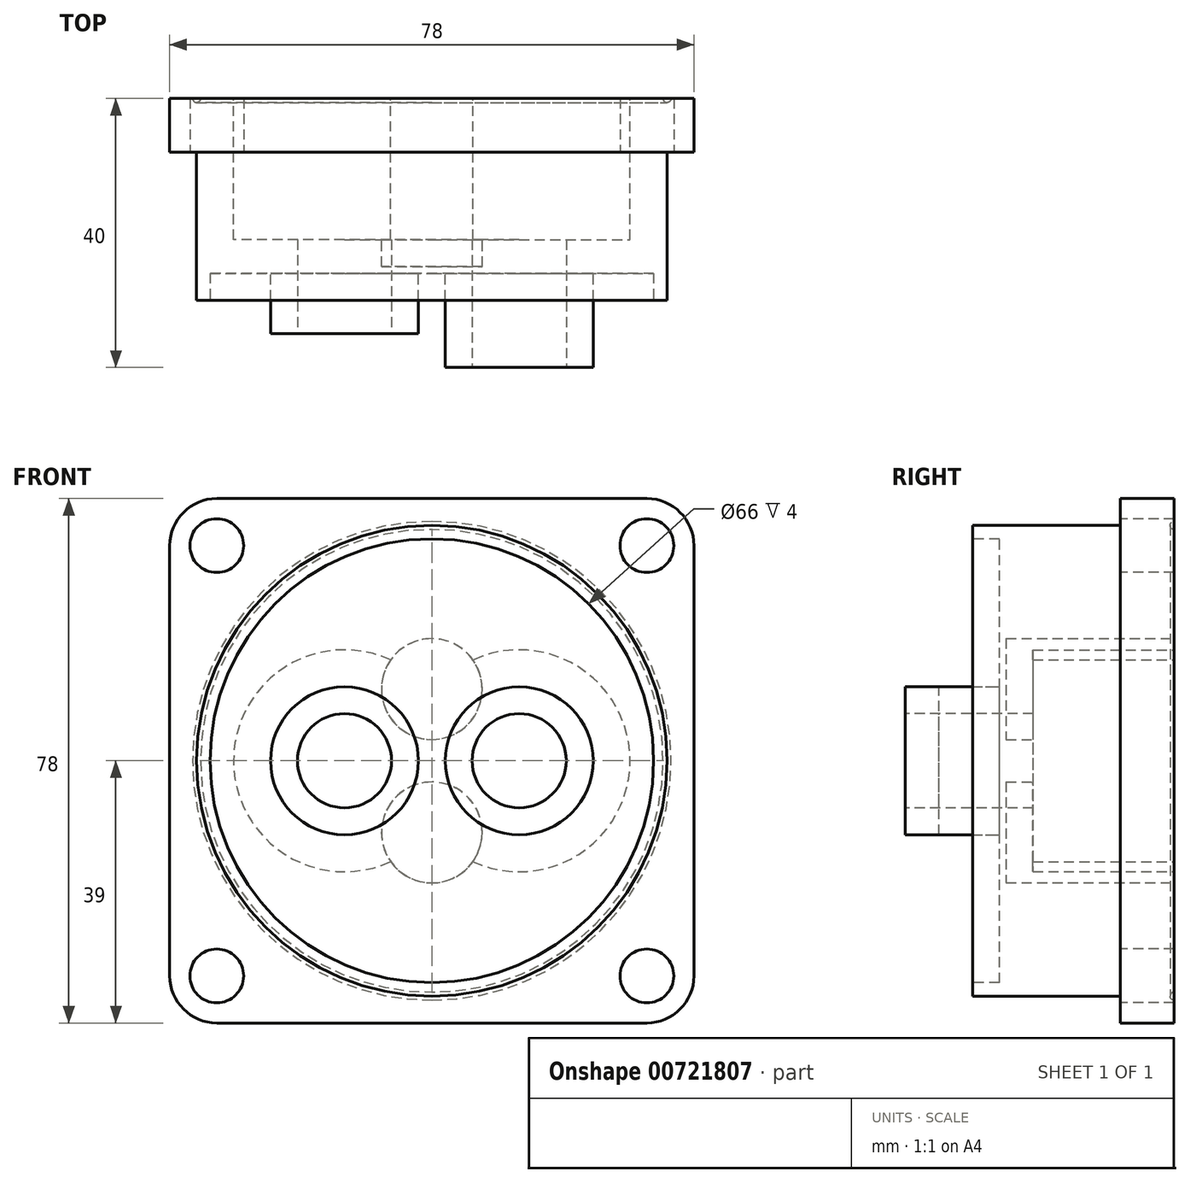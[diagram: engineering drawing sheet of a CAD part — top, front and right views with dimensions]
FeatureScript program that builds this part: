
annotation { "Feature Type Name" : "Feature", "Feature Type Description" : "" }
export const myFeature = defineFeature(function(context is Context, id is Id, definition is map)
    precondition{}
    {
        {
            var Q0;
            Q0=qCreatedBy(makeId("Front.planeOp"),FACE);
            var sketch = newSketch(context, id + "F0", { "sketchPlane" : qUnion([Q0])});
            skLineSegment(sketch, "E0.bottom", {"start": v(-39, 0) * mm, "end": v(39, 0) * mm});
            skLineSegment(sketch, "E0.top", {"start": v(-39, 78) * mm, "end": v(39, 78) * mm});
            skLineSegment(sketch, "E0.left", {"start": v(-39, 0) * mm, "end": v(-39, 78) * mm});
            skLineSegment(sketch, "E0.right", {"start": v(39, 0) * mm, "end": v(39, 78) * mm});
            skSolve(sketch);
        }
        {
            var Q0;
            Q0 = qSketchRegion(id + "F0", true);
            extrude(context, id + "F1", {"entities" : qUnion([Q0]), "depth" : 8 * mm, "offsetDistance" : 25 * mm});
        }
        {
            var Q0;
            Q0=makeQuery(id+"F1.opExtrude","SWEPT_EDGE",EDGE,{"disambiguationData":[OSD([sQuery(id+"F0.wireOp",EDGE,"E0.top"),sQuery(id+"F0.wireOp",EDGE,"E0.left")])]});
            var Q1;
            Q1=makeQuery(id+"F1.opExtrude","SWEPT_EDGE",EDGE,{"disambiguationData":[OSD([sQuery(id+"F0.wireOp",EDGE,"E0.top"),sQuery(id+"F0.wireOp",EDGE,"E0.right")])]});
            var Q2;
            Q2=makeQuery(id+"F1.opExtrude","SWEPT_EDGE",EDGE,{"disambiguationData":[OSD([sQuery(id+"F0.wireOp",EDGE,"E0.bottom"),sQuery(id+"F0.wireOp",EDGE,"E0.right")])]});
            var Q3;
            Q3=makeQuery(id+"F1.opExtrude","SWEPT_EDGE",EDGE,{"disambiguationData":[OSD([sQuery(id+"F0.wireOp",EDGE,"E0.bottom"),sQuery(id+"F0.wireOp",EDGE,"E0.left")])]});
            fillet(context, id + "F2", {"entities" : qUnion([Q0, Q1, Q2, Q3]), "radius" : 7 * mm, "tangentPropagation" : true, "allowEdgeOverflow" : false});
        }
        {
            var Q0;
            Q0=makeQuery(id+"F1.opExtrude","CAP_FACE",FACE,{"disambiguationData":[OSD([sQuery(id+"F0.wireOp",EDGE,"E0.bottom"),sQuery(id+"F0.wireOp",EDGE,"E0.top"),sQuery(id+"F0.wireOp",EDGE,"E0.left"),sQuery(id+"F0.wireOp",EDGE,"E0.right")])],"isStart":false});
            var sketch = newSketch(context, id + "F3", { "sketchPlane" : qUnion([Q0])});
            skCircle(sketch, "E1", {"center": v(-32, 71) * mm, "radius": 4 * mm});
            skCircle(sketch, "E2", {"center": v(32, 71) * mm, "radius": 4 * mm});
            skCircle(sketch, "E3", {"center": v(-32, 7) * mm, "radius": 4 * mm});
            skCircle(sketch, "E4", {"center": v(32, 7) * mm, "radius": 4 * mm});
            skCircle(sketch, "E5", {"center": v(0, 39) * mm, "radius": 35 * mm});
            skSolve(sketch);
        }
        {
            var Q0;
            Q0=makeQuery(id+"F3.imprint","IMPRINT",FACE,{"disambiguationData":[TD([[makeQuery(id+"F3.imprint","IMPRINT",EDGE,{"derivedFrom":sQuery(id+"F3.wireOp",EDGE,"E1")}),1.0]])]});
            var Q1;
            Q1=makeQuery(id+"F3.imprint","IMPRINT",FACE,{"disambiguationData":[TD([[makeQuery(id+"F3.imprint","IMPRINT",EDGE,{"derivedFrom":sQuery(id+"F3.wireOp",EDGE,"E2")}),1.0]])]});
            var Q2;
            Q2=makeQuery(id+"F3.imprint","IMPRINT",FACE,{"disambiguationData":[TD([[makeQuery(id+"F3.imprint","IMPRINT",EDGE,{"derivedFrom":sQuery(id+"F3.wireOp",EDGE,"E3")}),1.0]])]});
            var Q3;
            Q3=makeQuery(id+"F3.imprint","IMPRINT",FACE,{"disambiguationData":[TD([[makeQuery(id+"F3.imprint","IMPRINT",EDGE,{"derivedFrom":sQuery(id+"F3.wireOp",EDGE,"E4")}),1.0]])]});
            extrude(context, id + "F4", {"entities" : qUnion([Q0, Q1, Q2, Q3]), "operationType" : NewBodyOperationType.REMOVE, "endBound" : BoundingType.THROUGH_ALL, "oppositeDirection" : true, "depth" : 21 * mm, "offsetDistance" : 25 * mm});
        }
        {
            var Q0;
            Q0=makeQuery(id+"F1.opExtrude","CAP_FACE",FACE,{"disambiguationData":[OSD([sQuery(id+"F0.wireOp",EDGE,"E0.bottom"),sQuery(id+"F0.wireOp",EDGE,"E0.top"),sQuery(id+"F0.wireOp",EDGE,"E0.left"),sQuery(id+"F0.wireOp",EDGE,"E0.right")])],"isStart":false});
            var sketch = newSketch(context, id + "F5", { "sketchPlane" : qUnion([Q0])});
            skCircle(sketch, "E6", {"center": v(0, 39) * mm, "radius": 35 * mm});
            skSolve(sketch);
        }
        {
            var Q0;
            Q0=makeQuery(id+"F5.imprint","IMPRINT",FACE,{"disambiguationData":[TD([[makeQuery(id+"F5.imprint","IMPRINT",EDGE,{"derivedFrom":sQuery(id+"F5.wireOp",EDGE,"E6")}),1.0]])]});
            var Q1;
            Q1=sQuery(id+"F5.wireOp",EDGE,"E6");
            extrude(context, id + "F6", {"entities" : qUnion([Q0]), "operationType" : NewBodyOperationType.ADD, "surfaceEntities" : qUnion([Q1]), "depth" : 22 * mm, "offsetDistance" : 25 * mm});
        }
        {
            var Q0;
            Q0=makeQuery(id+"F6.opExtrude","CAP_FACE",FACE,{"disambiguationData":[OSD([sQuery(id+"F5.wireOp",EDGE,"E6")])],"isStart":false});
            var sketch = newSketch(context, id + "F7", { "sketchPlane" : qUnion([Q0])});
            skCircle(sketch, "E7", {"center": v(0, 39) * mm, "radius": 33 * mm});
            skSolve(sketch);
        }
        {
            var Q0;
            Q0=makeQuery(id+"F7.imprint","IMPRINT",FACE,{"disambiguationData":[TD([[makeQuery(id+"F7.imprint","IMPRINT",EDGE,{"derivedFrom":sQuery(id+"F7.wireOp",EDGE,"E7")}),1.0]])]});
            extrude(context, id + "F8", {"entities" : qUnion([Q0]), "operationType" : NewBodyOperationType.REMOVE, "oppositeDirection" : true, "depth" : 4 * mm, "offsetDistance" : 25 * mm});
        }
        {
            var Q0;
            Q0=makeQuery(id+"F1.opExtrude","CAP_FACE",FACE,{"disambiguationData":[OSD([sQuery(id+"F0.wireOp",EDGE,"E0.bottom"),sQuery(id+"F0.wireOp",EDGE,"E0.top"),sQuery(id+"F0.wireOp",EDGE,"E0.left"),sQuery(id+"F0.wireOp",EDGE,"E0.right")])],"isStart":true});
            var sketch = newSketch(context, id + "F9", { "sketchPlane" : qUnion([Q0])});
            skCircle(sketch, "E8", {"center": v(0, 39) * mm, "radius": 35 * mm});
            skSolve(sketch);
        }
        {
            var Q0;
            Q0=qCreatedBy(makeId("Right.planeOp"),FACE);
            var sketch = newSketch(context, id + "F10", { "sketchPlane" : qUnion([Q0])});
            skCircle(sketch, "E9", {"center": v(0, 74) * mm, "radius": 0.6 * mm});
            skLineSegment(sketch, "E10", {"start": v(0, 74.39) * mm, "end": v(0, 73.61) * mm});
            skSolve(sketch);
        }
        {
            var Q0;
            Q0 = qSketchRegion(id + "F10", true);
            var Q1;
            Q1=sQuery(id+"F9.wireOp",EDGE,"E8");
            sweep(context, id + "F11", {"operationType" : NewBodyOperationType.REMOVE, "profiles" : qUnion([Q0]), "path" : qUnion([Q1])});
        }
        {
            var Q0;
            Q0=makeQuery(id+"F11.boolean.opBoolean","SPLIT",FACE,{"disambiguationData":[TD([makeQuery(id+"F11.opSweep","SWEPT_FACE",FACE,{"disambiguationData":[OSD([sQuery(id+"F9.wireOp",EDGE,"E8"),sQuery(id+"F10.wireOp",EDGE,"E9")])]})])],"derivedFrom":makeQuery(id+"F1.opExtrude","CAP_FACE",FACE,{"disambiguationData":[OSD([sQuery(id+"F0.wireOp",EDGE,"E0.bottom"),sQuery(id+"F0.wireOp",EDGE,"E0.top"),sQuery(id+"F0.wireOp",EDGE,"E0.left"),sQuery(id+"F0.wireOp",EDGE,"E0.right")])],"isStart":true})});
            var sketch = newSketch(context, id + "F12", { "sketchPlane" : qUnion([Q0])});
            skCircle(sketch, "E11", {"center": v(13, 39) * mm, "radius": 16.5 * mm});
            skCircle(sketch, "E12.MirrorC", {"center": v(-13, 39) * mm, "radius": 16.5 * mm});
            skPoint(sketch, "E13", {"position": v(0, 49.16) * mm});
            skPoint(sketch, "E14", {"position": v(0, 28.84) * mm});
            skPoint(sketch, "E15", {"position": v(-1.86, 51.17) * mm});
            skSolve(sketch);
        }
        {
            var Q0;
            Q0 = qSketchRegion(id + "F12", true);
            extrude(context, id + "F13", {"entities" : qUnion([Q0]), "operationType" : NewBodyOperationType.REMOVE, "oppositeDirection" : true, "depth" : 21 * mm, "offsetDistance" : 25 * mm});
        }
        {
            var Q0;
            Q0=makeQuery(id+"F11.boolean.opBoolean","SPLIT",FACE,{"disambiguationData":[TD([makeQuery(id+"F11.opSweep","SWEPT_FACE",FACE,{"disambiguationData":[OSD([sQuery(id+"F9.wireOp",EDGE,"E8"),sQuery(id+"F10.wireOp",EDGE,"E9")])]})])],"derivedFrom":makeQuery(id+"F1.opExtrude","CAP_FACE",FACE,{"disambiguationData":[OSD([sQuery(id+"F0.wireOp",EDGE,"E0.bottom"),sQuery(id+"F0.wireOp",EDGE,"E0.top"),sQuery(id+"F0.wireOp",EDGE,"E0.left"),sQuery(id+"F0.wireOp",EDGE,"E0.right")])],"isStart":true})});
            var sketch = newSketch(context, id + "F14", { "sketchPlane" : qUnion([Q0])});
            skCircle(sketch, "E16", {"center": v(0, 28.34) * mm, "radius": 7.5 * mm});
            skCircle(sketch, "E17", {"center": v(0, 49.66) * mm, "radius": 7.5 * mm});
            skSolve(sketch);
        }
        {
            var Q0;
            Q0 = qSketchRegion(id + "F14", true);
            extrude(context, id + "F15", {"entities" : qUnion([Q0]), "operationType" : NewBodyOperationType.REMOVE, "oppositeDirection" : true, "depth" : 25 * mm, "offsetDistance" : 25 * mm});
        }
        {
            var Q0;
            Q0=makeQuery(id+"F8.boolean.opBoolean","COPY",FACE,{"derivedFrom":makeQuery(id+"F8.opExtrude","CAP_FACE",FACE,{"disambiguationData":[OSD([sQuery(id+"F7.wireOp",EDGE,"E7")])],"isStart":false})});
            var sketch = newSketch(context, id + "F16", { "sketchPlane" : qUnion([Q0])});
            skCircle(sketch, "E18", {"center": v(13, 39) * mm, "radius": 11 * mm});
            skSolve(sketch);
        }
        {
            var Q0;
            Q0=makeQuery(id+"F16.imprint","IMPRINT",FACE,{"disambiguationData":[TD([[makeQuery(id+"F16.imprint","IMPRINT",EDGE,{"derivedFrom":sQuery(id+"F16.wireOp",EDGE,"E18")}),1.0]])]});
            extrude(context, id + "F17", {"entities" : qUnion([Q0]), "operationType" : NewBodyOperationType.ADD, "depth" : 14 * mm, "offsetDistance" : 25 * mm});
        }
        {
            var Q0;
            Q0=makeQuery(id+"F8.boolean.opBoolean","COPY",FACE,{"derivedFrom":makeQuery(id+"F8.opExtrude","CAP_FACE",FACE,{"disambiguationData":[OSD([sQuery(id+"F7.wireOp",EDGE,"E7")])],"isStart":false})});
            var sketch = newSketch(context, id + "F18", { "sketchPlane" : qUnion([Q0])});
            skCircle(sketch, "E19", {"center": v(-13, 39) * mm, "radius": 11 * mm});
            skSolve(sketch);
        }
        {
            var Q0;
            Q0 = qSketchRegion(id + "F18", true);
            extrude(context, id + "F19", {"entities" : qUnion([Q0]), "operationType" : NewBodyOperationType.ADD, "depth" : 9 * mm, "offsetDistance" : 25 * mm});
        }
        {
            var Q0;
            Q0=makeQuery(id+"F19.opExtrude","CAP_FACE",FACE,{"disambiguationData":[OSD([sQuery(id+"F18.wireOp",EDGE,"E19")])],"isStart":false});
            var sketch = newSketch(context, id + "F20", { "sketchPlane" : qUnion([Q0])});
            skCircle(sketch, "E20", {"center": v(-13, 39) * mm, "radius": 7 * mm});
            skSolve(sketch);
        }
        {
            var Q0;
            Q0=makeQuery(id+"F20.imprint","IMPRINT",FACE,{"disambiguationData":[TD([[makeQuery(id+"F20.imprint","IMPRINT",EDGE,{"derivedFrom":sQuery(id+"F20.wireOp",EDGE,"E20")}),1.0]])]});
            var Q1;
            Q1=sQuery(id+"F20.wireOp",EDGE,"E20");
            extrude(context, id + "F21", {"entities" : qUnion([Q0]), "operationType" : NewBodyOperationType.REMOVE, "surfaceEntities" : qUnion([Q1]), "endBound" : BoundingType.THROUGH_ALL, "oppositeDirection" : true, "depth" : 25 * mm, "offsetDistance" : 25 * mm});
        }
        {
            var Q0;
            Q0=makeQuery(id+"F17.opExtrude","CAP_FACE",FACE,{"disambiguationData":[OSD([sQuery(id+"F16.wireOp",EDGE,"E18")])],"isStart":false});
            var sketch = newSketch(context, id + "F22", { "sketchPlane" : qUnion([Q0])});
            skCircle(sketch, "E21", {"center": v(13, 39) * mm, "radius": 7 * mm});
            skSolve(sketch);
        }
        {
            var Q0;
            Q0 = qSketchRegion(id + "F22", true);
            extrude(context, id + "F23", {"entities" : qUnion([Q0]), "operationType" : NewBodyOperationType.REMOVE, "endBound" : BoundingType.THROUGH_ALL, "oppositeDirection" : true, "depth" : 25 * mm, "offsetDistance" : 25 * mm});
        }
    });
